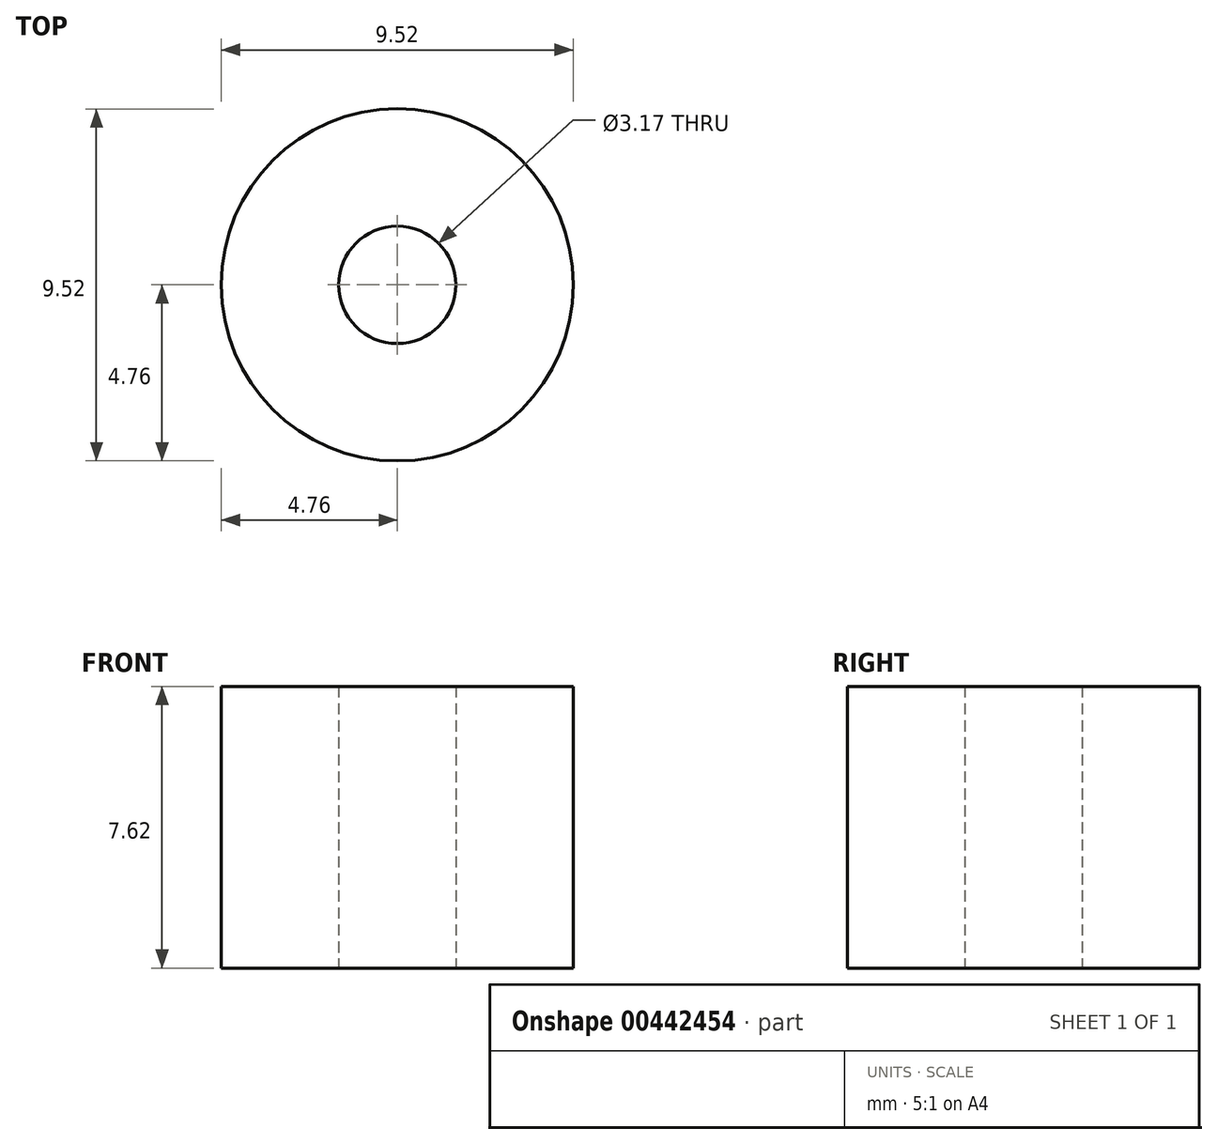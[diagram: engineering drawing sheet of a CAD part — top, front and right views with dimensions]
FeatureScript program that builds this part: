
annotation { "Feature Type Name" : "Feature", "Feature Type Description" : "" }
export const myFeature = defineFeature(function(context is Context, id is Id, definition is map)
    precondition{}
    {
        {
            var Q0;
            Q0=qCreatedBy(makeId("Top.planeOp"),FACE);
            var sketch = newSketch(context, id + "F0", { "sketchPlane" : qUnion([Q0])});
            skCircle(sketch, "E0", {"center": v(0, 0) * mm, "radius": 4.76 * mm});
            skCircle(sketch, "E1", {"center": v(0, 0) * mm, "radius": 1.59 * mm});
            skSolve(sketch);
        }
        {
            var Q0;
            Q0 = qSketchRegion(id + "F0", true);
            extrude(context, id + "F1", {"entities" : qUnion([Q0]), "depth" : 7.62 * mm});
        }
    });
